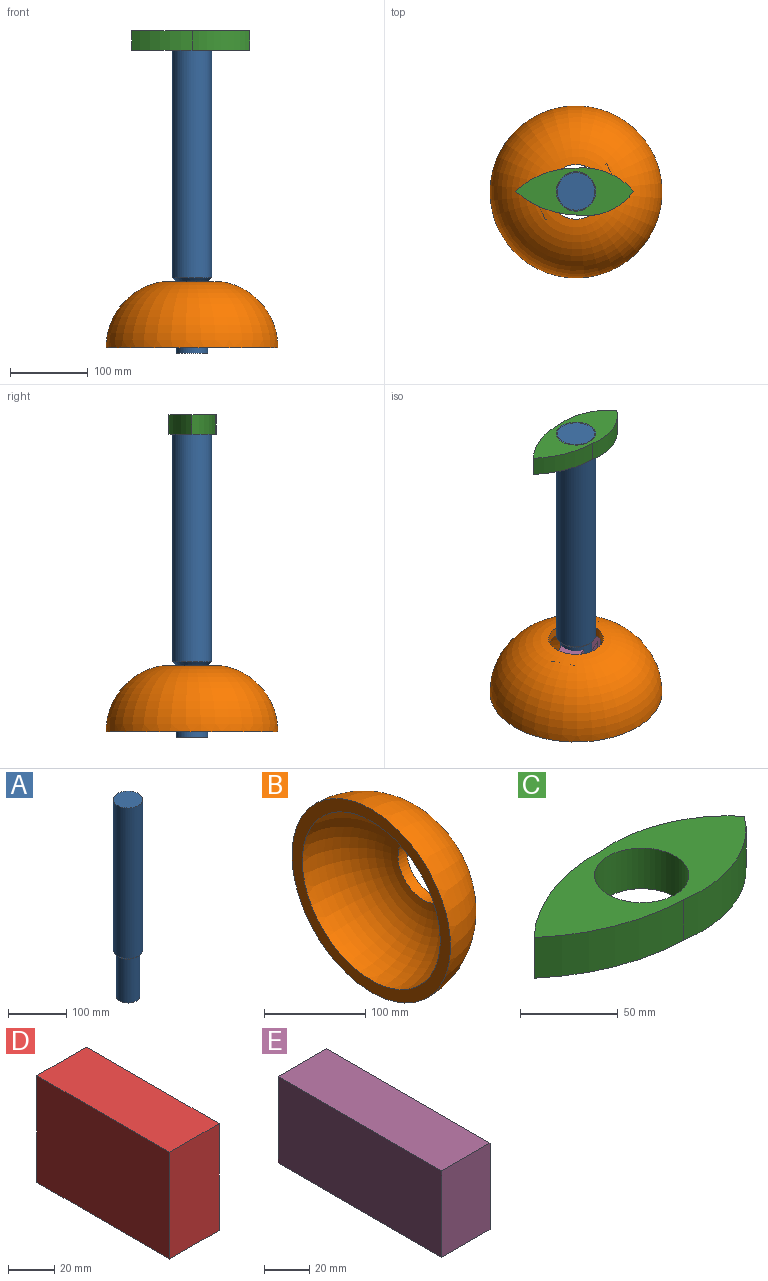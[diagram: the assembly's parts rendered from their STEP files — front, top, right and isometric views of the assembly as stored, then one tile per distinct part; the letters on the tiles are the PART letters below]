
ASSEMBLY  parts=5 mates=4
PART A: 5 faces, bbox 50.8x50.8x415.1 mm
  f0: cylinder r=25.4mm len=317.59mm, axis (0,0,1), area 50685.3mm2, adj f1,f2
  f1: plane 50.8x50.8mm, normal (0,0,1), area 2026.8mm2, adj f0
  f2: cone r=25.4mm half-angle=45deg, axis (0,0,1), area 1031.9mm2, adj f0,f3
  f3: cylinder r=20.32mm len=92.41mm, axis (0,0,1), area 11798mm2, adj f2,f4
  f4: plane 40.64x40.64mm, normal (0,0,-1), area 1297.2mm2, adj f3
PART B: 4 faces, bbox 84.9x221.3x221.3 mm
  f0: torus R=25.69mm, axis (-1,0,0), area 65388.2mm2, adj f1,f3
  f1: plane 221.27x221.27mm, normal (-1,0,0), area 9352.4mm2, adj f0,f2
  f2: torus R=26.42mm, axis (-1,0,0), area 49118mm2, adj f1,f3
  f3: cylinder r=35.22mm len=70.43mm, axis (-1,0,0), area 2746.6mm2, adj f0,f2
PART C: 7 faces, bbox 151.9x61.8x25.4 mm
  f0: cylinder r=123.47mm len=77.76mm, axis (0,0,-1), area 2162.6mm2, adj f1,f3,f4,f5
  f1: cylinder r=76.41mm len=74.13mm, axis (0,0,-1), area 2141.4mm2, adj f0,f2,f4,f5
  f2: cylinder r=85.26mm len=74.13mm, axis (0,0,-1), area 2114mm2, adj f1,f3,f4,f5
  f3: cylinder r=108.87mm len=77.76mm, axis (0,0,-1), area 2172.2mm2, adj f0,f2,f4,f5
  f4: plane 151.89x61.77mm, normal (0,0,1), area 4772.8mm2, adj f0,f1,f2,f3,f6
  f5: plane 151.89x61.77mm, normal (0,0,-1), area 4772.8mm2, adj f0,f1,f2,f3,f6
  f6: cylinder r=24.13mm len=48.26mm, axis (0,0,-1), area 3851mm2, adj f4,f5
PART D: 6 faces, bbox 30.2x81x56.4 mm
  f0: plane 80.96x30.22mm, normal (0,0,1), area 2446.3mm2, adj f1,f3,f4,f5
  f1: plane 56.37x30.22mm, normal (0,1,0), area 1703.3mm2, adj f0,f2,f4,f5
  f2: plane 80.96x30.22mm, normal (0,0,-1), area 2446.3mm2, adj f1,f3,f4,f5
  f3: plane 56.37x30.22mm, normal (0,-1,0), area 1703.3mm2, adj f0,f2,f4,f5
  f4: plane 80.96x56.37mm, normal (1,0,0), area 4563.2mm2, adj f0,f1,f2,f3
  f5: plane 80.96x56.37mm, normal (-1,0,0), area 4563.2mm2, adj f0,f1,f2,f3
PART E: 6 faces, bbox 30.2x102.1x46.7 mm
  f0: plane 102.11x30.22mm, normal (0,0,-1), area 3085.7mm2, adj f1,f3,f4,f5
  f1: plane 46.73x30.22mm, normal (0,-1,0), area 1412.1mm2, adj f0,f2,f4,f5
  f2: plane 102.11x30.22mm, normal (0,0,1), area 3085.7mm2, adj f1,f3,f4,f5
  f3: plane 46.73x30.22mm, normal (0,1,0), area 1412.1mm2, adj f0,f2,f4,f5
  f4: plane 102.11x46.73mm, normal (1,0,0), area 4771.9mm2, adj f0,f1,f2,f3
  f5: plane 102.11x46.73mm, normal (-1,0,0), area 4771.9mm2, adj f0,f1,f2,f3
PLACE A t=(-28.52,111.69,0)mm fixed
PLACE B rot(axis=(-0.47,-0.75,-0.47),106.4deg) t=(-28.52,111.69,-428.07)mm
PLACE C t=(-28.52,111.69,-12.7)mm
PLACE D rot(axis=(0,0,-1),64.2deg) t=(-7.61,161.38,-77.76)mm
PLACE E rot(axis=(0,0,-1),64.2deg) t=(-89.99,121.48,-600.6)mm
MATE revolute B.f0 <-> A.f0  axis (0,0,-1) through (-28.52,111.69,-322.67)mm
MATE fastened C.f6 <-> A.f0  axis (0,0,1) through (-28.52,111.69,0)mm
MATE fastened D.f2 <-> B.f0  axis (0,0,-1) through (-28.52,111.69,-407.57)mm
MATE fastened E.f5 <-> D.f5  axis (-0.44,0.9,0) through (-35.11,125.29,-351.21)mm
